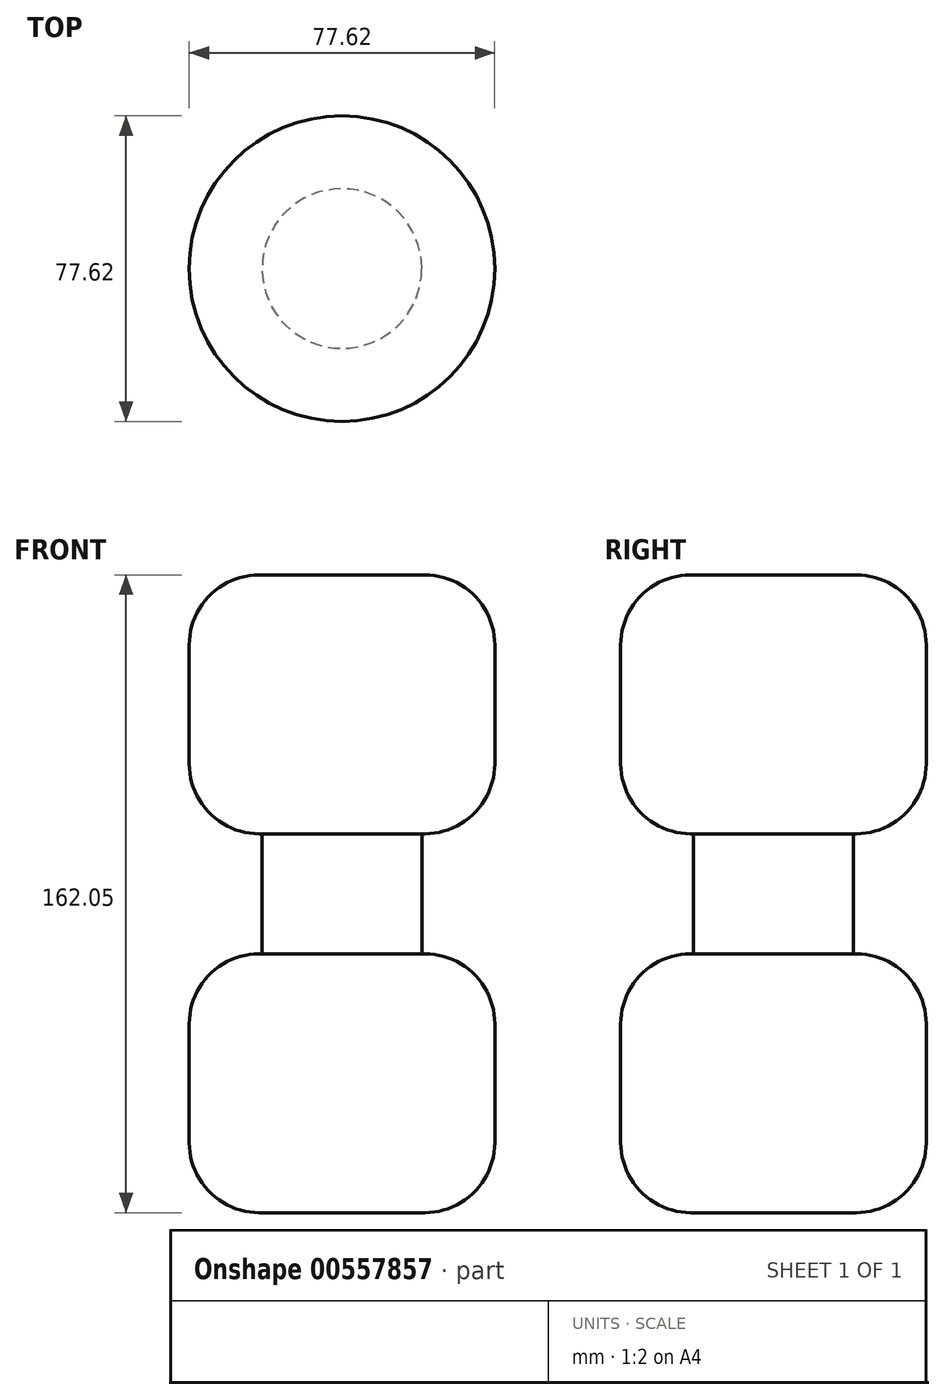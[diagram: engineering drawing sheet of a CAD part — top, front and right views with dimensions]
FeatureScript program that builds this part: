
annotation { "Feature Type Name" : "Feature", "Feature Type Description" : "" }
export const myFeature = defineFeature(function(context is Context, id is Id, definition is map)
    precondition{}
    {
        {
            var Q0;
            Q0=qCreatedBy(makeId("Top.planeOp"),FACE);
            var sketch = newSketch(context, id + "F0", { "sketchPlane" : qUnion([Q0])});
            skCircle(sketch, "E0", {"center": v(0, 0) * mm, "radius": 38.81 * mm});
            skSolve(sketch);
        }
        {
            var Q0;
            Q0=makeQuery(id+"F0.imprint","IMPRINT",FACE,{"disambiguationData":[TD([[makeQuery(id+"F0.imprint","IMPRINT",EDGE,{"derivedFrom":sQuery(id+"F0.wireOp",EDGE,"E0")}),1.0]])]});
            extrude(context, id + "F1", {"entities" : qUnion([Q0]), "depth" : 65.8 * mm, "offsetDistance" : 25.4 * mm});
        }
        {
            var Q0;
            Q0=makeQuery(id+"F1.opExtrude","CAP_FACE",FACE,{"disambiguationData":[OSD([sQuery(id+"F0.wireOp",EDGE,"E0")])],"isStart":false});
            var sketch = newSketch(context, id + "F2", { "sketchPlane" : qUnion([Q0])});
            skCircle(sketch, "E1", {"center": v(0, 0) * mm, "radius": 20.28 * mm});
            skSolve(sketch);
        }
        {
            var Q0;
            Q0=makeQuery(id+"F2.imprint","IMPRINT",FACE,{"disambiguationData":[TD([[makeQuery(id+"F2.imprint","IMPRINT",EDGE,{"derivedFrom":sQuery(id+"F2.wireOp",EDGE,"E1")}),1.0]])]});
            extrude(context, id + "F3", {"entities" : qUnion([Q0]), "operationType" : NewBodyOperationType.ADD, "depth" : 15.24 * mm, "offsetDistance" : 25.4 * mm});
        }
        {
            var Q0;
            Q0=makeQuery(id+"F1.opExtrude","SWEPT_BODY",BODY,{"disambiguationData":[OSD([sQuery(id+"F0.wireOp",EDGE,"E0")])]});
            var Q1;
            Q1=makeQuery(id+"F3.opExtrude","CAP_FACE",FACE,{"disambiguationData":[OSD([sQuery(id+"F2.wireOp",EDGE,"E1")])],"isStart":false});
            mirror(context, id + "F4", {"operationType" : NewBodyOperationType.ADD, "entities" : qUnion([Q0]), "mirrorPlane" : qUnion([Q1])});
        }
        {
            var Q0;
            Q0=makeQuery(id+"F4.opPattern","COPY",FACE,{"derivedFrom":makeQuery(id+"F1.opExtrude","SWEPT_FACE",FACE,{"disambiguationData":[OSD([sQuery(id+"F0.wireOp",EDGE,"E0")])]}),"instanceName":"1"});
            var Q1;
            Q1=makeQuery(id+"F1.opExtrude","SWEPT_FACE",FACE,{"disambiguationData":[OSD([sQuery(id+"F0.wireOp",EDGE,"E0")])]});
            fillet(context, id + "F5", {"entities" : qUnion([Q0, Q1]), "radius" : 17.78 * mm, "tangentPropagation" : true, "allowEdgeOverflow" : false});
        }
    });
